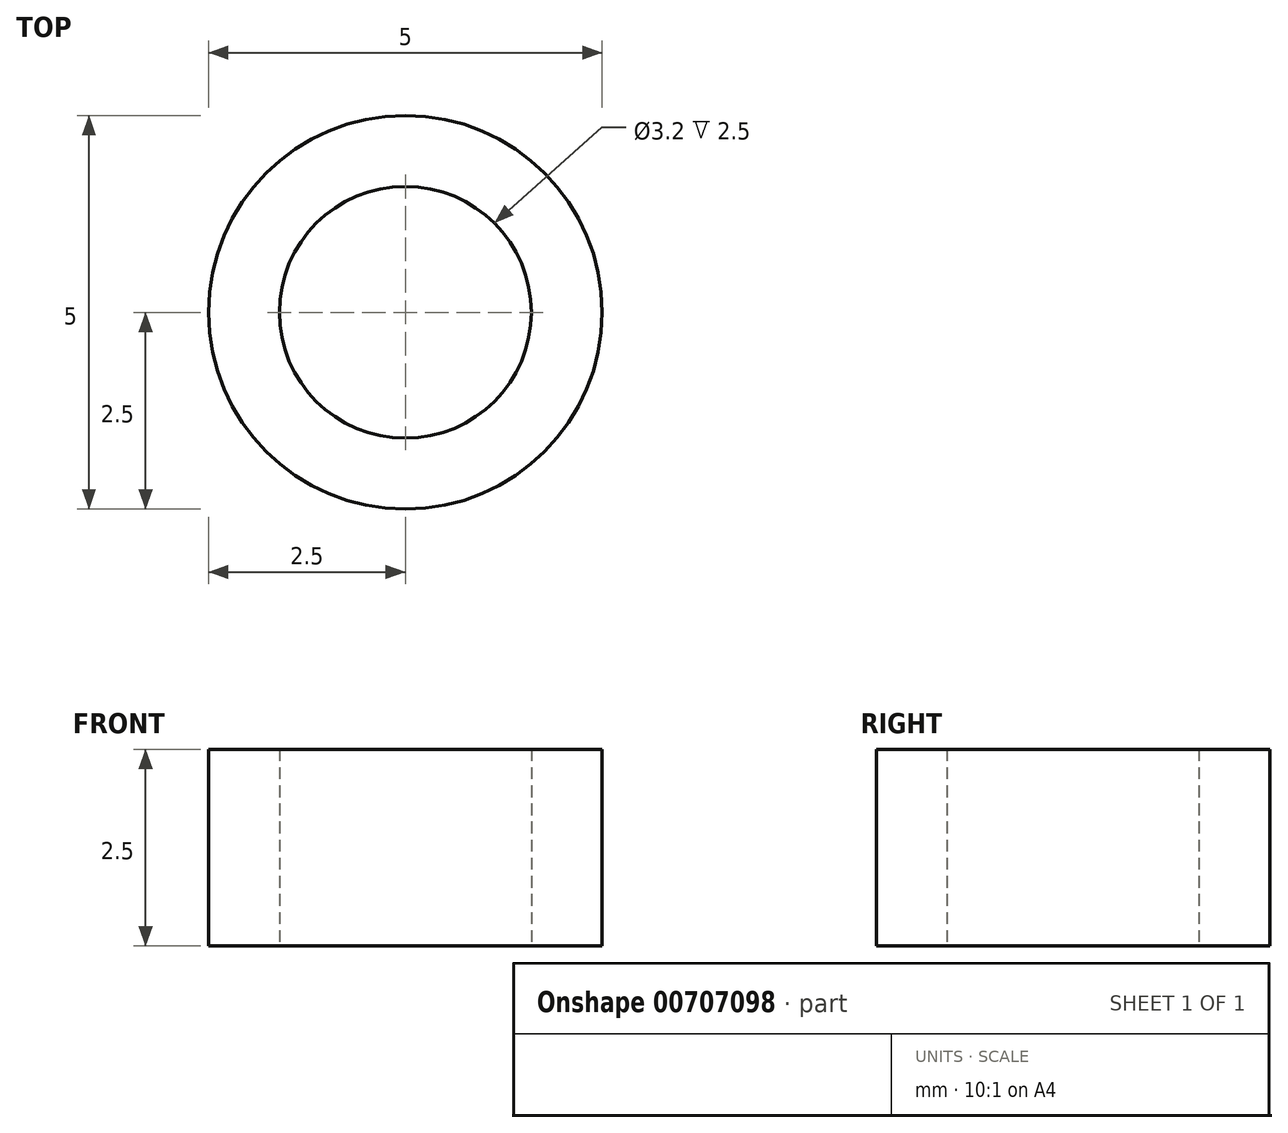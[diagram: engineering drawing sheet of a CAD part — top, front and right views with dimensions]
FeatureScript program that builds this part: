
annotation { "Feature Type Name" : "Feature", "Feature Type Description" : "" }
export const myFeature = defineFeature(function(context is Context, id is Id, definition is map)
    precondition{}
    {
        {
            var Q0;
            Q0=qCreatedBy(makeId("Top.planeOp"),FACE);
            var sketch = newSketch(context, id + "F0", { "sketchPlane" : qUnion([Q0])});
            skCircle(sketch, "E0", {"center": v(0, 0) * mm, "radius": 1.6 * mm});
            skCircle(sketch, "E1", {"center": v(0, 0) * mm, "radius": 2.5 * mm});
            skSolve(sketch);
        }
        {
            var Q0;
            Q0=makeQuery(id+"F0.imprint","IMPRINT",FACE,{"disambiguationData":[TD([[makeQuery(id+"F0.imprint","IMPRINT",EDGE,{"derivedFrom":sQuery(id+"F0.wireOp",EDGE,"E0")}),-1.0]])]});
            extrude(context, id + "F1", {"entities" : qUnion([Q0]), "flatOperationType" : FlatOperationType.REMOVE, "depth" : 2.5 * mm, "offsetDistance" : 25 * mm, "domain" : OperationDomain.MODEL});
        }
    });
